# Revit family: Shower-Side_Panel-KOHLER-COMPOSED-1.1922.024_1
name_source: partatom
category: Specialty Equipment
revit_build: Autodesk Revit 2017 (Build: 20160225_1515(x64)
units: mm (PartAtom-declared; Revit-internal decimal feet)

## family parameters
Cut with Voids When Loaded = No
Host = Face
OmniClass Number = 23.31.17.17
OmniClass Title = Shower Enclosures
Part Type = Normal
Room Calculation Point = No
Round Connector Dimension = Use Diameter
Shared = No

## types (1)
- Polished Chrome
    ADA Compliant = No
    Assembly Code = C1030200
    Date Modified = 10/08/2021
    Default Elevation = 0"
    Description = COMPOSED SLDG ENCLOSURE SIDE PANEL 800MM
    Finish = Kohler-Metal-CP-Polished_Chrome
    Height = 78 3/4"
    Length = 1 3/8"
    Manufacturer = KOHLER Co.
    Master Format 2014 = 10 28 19.16
    Master Format 2014 Name = Shower Doors
    Material = Anodized Aluminum
    Model = 1.1922.024
    Product Name = COMPOSED
    Type = 1
    URL = https://www.kohler.co.uk
    WaterSense Certified = No

## geometry (parser evidence)
native form markers: Sweep x4
no freeform markers — native parametric forms only
